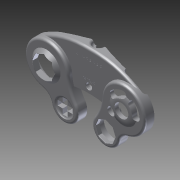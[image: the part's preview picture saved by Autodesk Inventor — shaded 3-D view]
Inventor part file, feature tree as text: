
AUTODESK INVENTOR PART (.ipt)
format: ipt  version: 2012 SP1 (Build 160190100, 190)  size: 1,422,848 bytes
history: native  units: in
note: dims shown in document units (in); Inventor stores cm internally (conversion verified against a paired STEP export)
features: extrude x40, sketch x40, fillet x5, chamfer x2, shell x1
ambient origin geometry x8: Origin, YZ Plane, XZ Plane, XY Plane, X Axis, Y Axis, Z Axis, Center Point
bodies: Solid1 (feature_tree)
feature tree (88):
  extrude  "Extrusion1"  Depth=1.9in
  extrude  "Extrusion2"  Depth=0.24in TaperAngle=0.0deg
  extrude  "Extrusion3"  Depth=0.18in TaperAngle=0.0deg
  extrude  "Extrusion4"  Depth=0.24in
  extrude  "Extrusion5"  Depth=1.0in TaperAngle=0.0deg
  extrude  "Extrusion6"  Depth=0.42in TaperAngle=0.0deg
  fillet  "Fillet1"  Radius=0.5in
  extrude  "Extrusion7"  Depth=1.17in
  fillet  "Fillet2"  Radius=0.07in
  extrude  "Extrusion8"  Depth=0.4375in
  extrude  "Extrusion9"  Depth=0.4375in
  extrude  "Extrusion10"  Depth=0.072in TaperAngle=0.0deg
  extrude  "Extrusion11"  Depth=1.0in TaperAngle=0.0deg
  extrude  "Extrusion12"  Depth=0.278in
  extrude  "Extrusion13"  Depth=0.278in
  chamfer  "Chamfer1"  Distance=0.04in
  extrude  "Extrusion14"  Depth=0.16in TaperAngle=0.0deg
  extrude  "Extrusion15"  Depth=0.83in
  fillet  "Fillet3"  Radius=0.05in
  extrude  "Extrusion16"  Depth=0.11in
  extrude  "Extrusion17"  Depth=0.22in
  extrude  "Extrusion18"  Depth=0.15in
  extrude  "Extrusion19"  Depth=0.16in TaperAngle=0.0deg
  fillet  "Fillet4"  Radius=0.44in
  extrude  "Extrusion20"  Depth=0.11in
  extrude  "Extrusion21"  Depth=0.1in
  extrude  "Extrusion22"  Depth=0.25in TaperAngle=0.0deg
  extrude  "Extrusion23"  Depth=0.25in
  shell  "Shell1"  Thickness=2.0in
  extrude  "Extrusion24"  Depth=0.125in TaperAngle=0.0deg
  extrude  "Extrusion25"  Depth=1.0in TaperAngle=0.0deg
  extrude  "Extrusion26"  Depth=1.0in TaperAngle=0.0deg
  extrude  "Extrusion27"  Depth=1.0in TaperAngle=0.0deg
  extrude  "Extrusion28"  Depth=1.0in TaperAngle=0.0deg
  extrude  "Extrusion29"  Depth=1.0in TaperAngle=0.0deg
  extrude  "Extrusion30"  Depth=1.0in TaperAngle=0.0deg
  extrude  "Extrusion31"  Depth=0.0025in TaperAngle=0.0deg
  extrude  "Extrusion32"  Depth=0.02in
  extrude  "Extrusion33"  Depth=2.0in TaperAngle=0.0deg
  extrude  "Extrusion34"  Depth=1.0in
  extrude  "Extrusion35"  Depth=0.57in
  extrude  "Extrusion36"  Depth=0.1in
  chamfer  "Chamfer2"  Distance=0.086in
  extrude  "Extrusion37"  Depth=0.069in
  extrude  "Extrusion38"  Depth=0.025in
  fillet  "Fillet5"  Radius=0.022in
  extrude  "Extrusion39"  Depth=0.01in
  extrude  "Extrusion40"  Depth=0.01in TaperAngle=0.0deg
  sketch  "Sketch1"  dims[d6=1.9in d7=1.9in]
  sketch  "Sketch2"  dims[d13=1.18in d14=0.24in d15=0.0in]
  sketch  "Sketch3"  dims[d16=0.18in d17=0.0in d18=0.18in d19=0.0in]
  sketch  "Sketch4"  dims[d23=0.74in d24=0.24in]
  sketch  "Sketch5"  dims[d25=1.0in d26=0.0in d27=1.0in d28=0.0in]
  sketch  "Sketch6"  dims[d29=4.18in d36=0.42in d37=0.0in d38=0.5in]
  sketch  "Sketch7"  dims[d39=0.6in d40=1.17in d41=0.07in d42=0.0in]
  sketch  "Sketch8"  dims[d43=0.5in d44=0.4375in]
  sketch  "Sketch9"  dims[d45=0.4375in d46=0.4375in]
  sketch  "Sketch10"  dims[d47=0.4375in d48=0.072in d49=0.0in]
  sketch  "Sketch11"  dims[d50=0.36in d51=1.0in d52=0.056in d53=0.0in d54=0.0in]
  sketch  "Sketch12"  dims[d55=0.278in d56=0.278in]
  sketch  "Sketch13"  dims[d57=1.0in d58=0.07in d59=0.0in d60=0.0in d61=0.278in]
  sketch  "Sketch15"  dims[d64=1.0in d65=0.07in d66=0.0in d67=0.0in]
  sketch  "Sketch16"  dims[d68=0.26in]
  sketch  "Sketch17"  dims[d69=0.26in d70=0.04in d71=0.0in]
  sketch  "Sketch18"  dims[d72=1.225in d73=0.16in d74=0.0in]
  sketch  "Sketch19"  dims[d76=0.16in d77=0.125in d78=45.0deg d79=0.83in d80=0.05in d81=0.0in]
  sketch  "Sketch20"  dims[d82=0.33in d83=0.11in]
  sketch  "Sketch21"  dims[d84=0.22in d85=0.22in]
  sketch  "Sketch22"  dims[d86=0.1in d87=0.0in d88=0.15in]
  sketch  "Sketch23"  dims[d89=0.16in d90=0.0in d91=0.16in d92=0.0in d93=0.44in]
  sketch  "Sketch24"  dims[d94=0.15in d95=0.0in d97=0.11in]
  sketch  "Sketch25"  dims[d98=0.075in d99=0.0in d100=0.1in]
  sketch  "Sketch26"  dims[d101=0.19in d102=0.25in d103=0.0in]
  sketch  "Sketch27"  dims[d105=0.25in d107=0.25in d108=2.0in d109=0.0in]
  sketch  "Sketch28"  dims[d110=0.9in d111=0.0in d112=0.125in d113=0.0in]
  sketch  "Sketch29"  dims[d114=0.1in d115=1.0in d116=0.0in]
  sketch  "Sketch30"  dims[d117=1.0in d118=0.0in d119=1.0in d120=0.0in]
  sketch  "Sketch31"  dims[d121=1.0in d122=0.0in d123=1.0in d124=0.0in]
  sketch  "Sketch32"  dims[d125=1.0in d126=0.0in d127=1.0in d128=0.0in]
  sketch  "Sketch33"  dims[d129=1.0in d130=0.0in d131=1.0in d132=0.0in]
  sketch  "Sketch34"  dims[d133=1.0in d134=0.0in d135=1.0in d136=0.0in]
  sketch  "Sketch35"  dims[d137=1.0in d138=0.0in d140=0.0025in d141=0.0in]
  sketch  "Sketch36"  dims[d142=0.0125in d143=0.125in d144=45.0deg d145=0.02in]
  sketch  "Sketch37"  dims[d146=0.2in d147=0.0in d148=2.0in d149=0.0in]
  sketch  "Sketch38"  dims[d150=0.1in d151=1.0in]
  sketch  "Sketch39"  dims[d152=0.57in d153=0.57in]
  sketch  "Sketch42"  dims[d154=0.01in d155=0.0in d156=0.1in]
  sketch  "Sketch43"  dims[d157=0.03in d158=0.086in d159=0.069in d160=0.025in d161=0.022in d162=0.01in d163=0.01in d164=0.0in]
